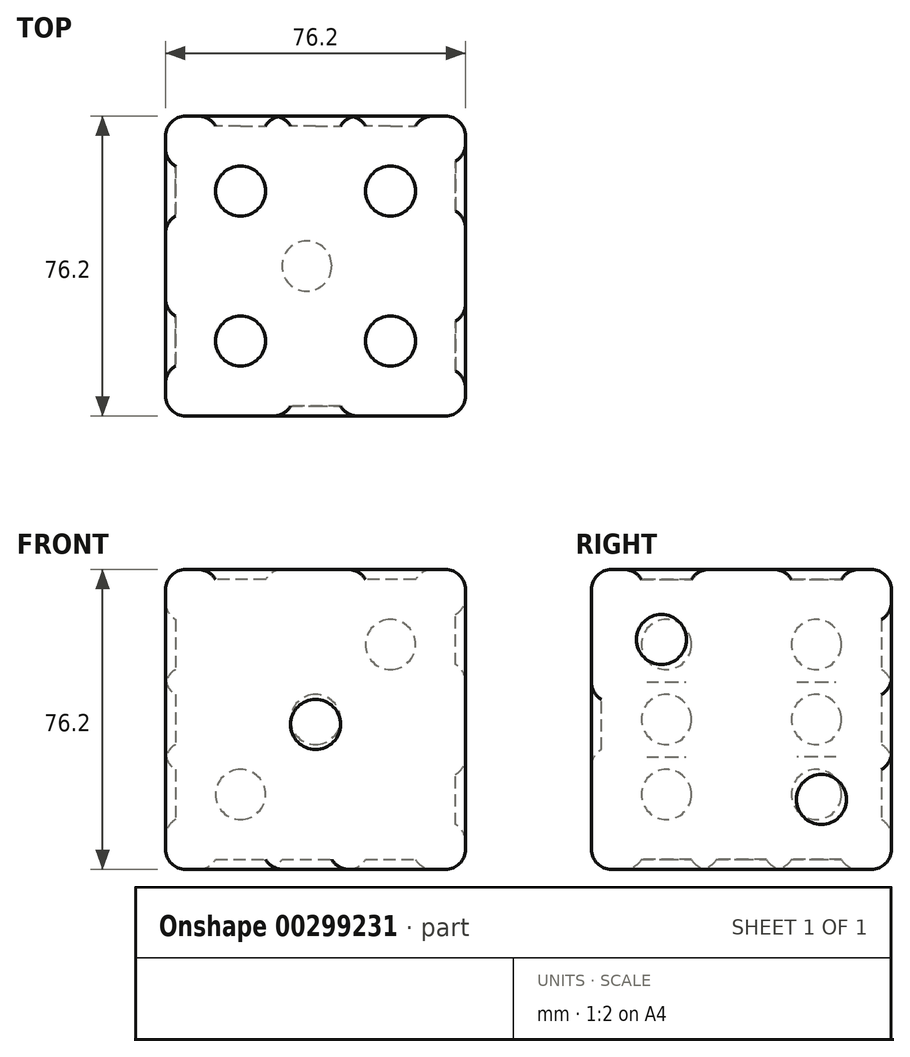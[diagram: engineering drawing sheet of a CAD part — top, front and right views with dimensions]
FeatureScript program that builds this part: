
annotation { "Feature Type Name" : "Feature", "Feature Type Description" : "" }
export const myFeature = defineFeature(function(context is Context, id is Id, definition is map)
    precondition{}
    {
        {
            var Q0;
            Q0=qCreatedBy(makeId("Front.planeOp"),FACE);
            var sketch = newSketch(context, id + "F0", { "sketchPlane" : qUnion([Q0])});
            skLineSegment(sketch, "E0", {"start": v(-45.03, 53.53) * mm, "end": v(31.17, 53.53) * mm});
            skLineSegment(sketch, "E1", {"start": v(31.17, 53.53) * mm, "end": v(31.17, -22.67) * mm});
            skLineSegment(sketch, "E2", {"start": v(31.17, -22.67) * mm, "end": v(-45.03, -22.67) * mm});
            skLineSegment(sketch, "E3", {"start": v(-45.03, -22.67) * mm, "end": v(-45.03, 53.53) * mm});
            skCircle(sketch, "E4", {"center": v(-6.93, 14.16) * mm, "radius": 6.35 * mm});
            skSolve(sketch);
        }
        {
            var Q0;
            Q0 = qSketchRegion(id + "F0", true);
            extrude(context, id + "F1", {"entities" : qUnion([Q0]), "depth" : 76.2 * mm});
        }
        {
            var Q0;
            Q0=makeQuery(id+"F0.imprint","IMPRINT",FACE,{"disambiguationData":[TD([[makeQuery(id+"F0.imprint","IMPRINT",EDGE,{"derivedFrom":sQuery(id+"F0.wireOp",EDGE,"E4")}),1.0]])]});
            extrude(context, id + "F2", {"entities" : qUnion([Q0]), "operationType" : NewBodyOperationType.ADD, "depth" : 73.66 * mm});
        }
        {
            var Q0;
            Q0=makeQuery(id+"F1.opExtrude","SWEPT_FACE",FACE,{"disambiguationData":[OSD([sQuery(id+"F0.wireOp",EDGE,"E1")])]});
            var sketch = newSketch(context, id + "F3", { "sketchPlane" : qUnion([Q0])});
            skCircle(sketch, "E5", {"center": v(-58.42, 35.75) * mm, "radius": 6.35 * mm});
            skCircle(sketch, "E6", {"center": v(-17.78, -4.9) * mm, "radius": 6.35 * mm});
            skSolve(sketch);
        }
        {
            var Q0;
            Q0=makeQuery(id+"F3.imprint","IMPRINT",FACE,{"disambiguationData":[TD([[makeQuery(id+"F3.imprint","IMPRINT",EDGE,{"derivedFrom":sQuery(id+"F3.wireOp",EDGE,"E5")}),1.0]])]});
            extrude(context, id + "F4", {"entities" : qUnion([Q0]), "operationType" : NewBodyOperationType.REMOVE, "oppositeDirection" : true, "depth" : 2.54 * mm});
        }
        {
            var Q0;
            Q0=makeQuery(id+"F3.imprint","IMPRINT",FACE,{"disambiguationData":[TD([[makeQuery(id+"F3.imprint","IMPRINT",EDGE,{"derivedFrom":sQuery(id+"F3.wireOp",EDGE,"E6")}),1.0]])]});
            extrude(context, id + "F5", {"entities" : qUnion([Q0]), "operationType" : NewBodyOperationType.REMOVE, "oppositeDirection" : true, "depth" : 2.54 * mm});
        }
        {
            var Q0;
            {var subQ0=sQuery(id+"F0.wireOp",EDGE,"E4");Q0=makeQuery(id+"F2.boolean.opBoolean","MERGE",FACE,{"derivedFrom":[makeQuery(id+"F1.opExtrude","CAP_FACE",FACE,{"disambiguationData":[OSD([sQuery(id+"F0.wireOp",EDGE,"E0"),sQuery(id+"F0.wireOp",EDGE,"E1"),sQuery(id+"F0.wireOp",EDGE,"E2"),sQuery(id+"F0.wireOp",EDGE,"E3"),subQ0])],"isStart":true}),makeQuery(id+"F2.opExtrude","CAP_FACE",FACE,{"disambiguationData":[OSD([subQ0])],"isStart":true})]});}
            var sketch = newSketch(context, id + "F6", { "sketchPlane" : qUnion([Q0])});
            skCircle(sketch, "E7", {"center": v(6.93, 15.43) * mm, "radius": 6.35 * mm});
            skPoint(sketch, "E7.centerSnap0", {"position": v(45.03, 15.43) * mm});
            skCircle(sketch, "E8", {"center": v(-12.12, 34.48) * mm, "radius": 6.35 * mm});
            skCircle(sketch, "E9", {"center": v(25.98, -3.62) * mm, "radius": 6.35 * mm});
            skSolve(sketch);
        }
        {
            var Q0;
            Q0=makeQuery(id+"F6.imprint","IMPRINT",FACE,{"disambiguationData":[TD([[makeQuery(id+"F6.imprint","IMPRINT",EDGE,{"derivedFrom":sQuery(id+"F6.wireOp",EDGE,"E7")}),1.0]])]});
            extrude(context, id + "F7", {"entities" : qUnion([Q0]), "operationType" : NewBodyOperationType.REMOVE, "oppositeDirection" : true, "depth" : 2.54 * mm});
        }
        {
            var Q0;
            Q0=makeQuery(id+"F6.imprint","IMPRINT",FACE,{"disambiguationData":[TD([[makeQuery(id+"F6.imprint","IMPRINT",EDGE,{"derivedFrom":sQuery(id+"F6.wireOp",EDGE,"E8")}),1.0]])]});
            extrude(context, id + "F8", {"entities" : qUnion([Q0]), "operationType" : NewBodyOperationType.REMOVE, "oppositeDirection" : true, "depth" : 2.54 * mm});
        }
        {
            var Q0;
            Q0=makeQuery(id+"F6.imprint","IMPRINT",FACE,{"disambiguationData":[TD([[makeQuery(id+"F6.imprint","IMPRINT",EDGE,{"derivedFrom":sQuery(id+"F6.wireOp",EDGE,"E9")}),1.0]])]});
            extrude(context, id + "F9", {"entities" : qUnion([Q0]), "operationType" : NewBodyOperationType.REMOVE, "oppositeDirection" : true, "depth" : 2.54 * mm});
        }
        {
            var Q0;
            Q0=makeQuery(id+"F1.opExtrude","SWEPT_FACE",FACE,{"disambiguationData":[OSD([sQuery(id+"F0.wireOp",EDGE,"E0")])]});
            var sketch = newSketch(context, id + "F10", { "sketchPlane" : qUnion([Q0])});
            skCircle(sketch, "E10", {"center": v(-25.98, -19.05) * mm, "radius": 6.35 * mm});
            skCircle(sketch, "E11", {"center": v(12.12, -19.05) * mm, "radius": 6.35 * mm});
            skCircle(sketch, "E12", {"center": v(-25.98, -57.15) * mm, "radius": 6.35 * mm});
            skCircle(sketch, "E13", {"center": v(12.12, -57.15) * mm, "radius": 6.35 * mm});
            skSolve(sketch);
        }
        {
            var Q0;
            Q0=makeQuery(id+"F10.imprint","IMPRINT",FACE,{"disambiguationData":[TD([[makeQuery(id+"F10.imprint","IMPRINT",EDGE,{"derivedFrom":sQuery(id+"F10.wireOp",EDGE,"E10")}),1.0]])]});
            var Q1;
            Q1=makeQuery(id+"F10.imprint","IMPRINT",FACE,{"disambiguationData":[TD([[makeQuery(id+"F10.imprint","IMPRINT",EDGE,{"derivedFrom":sQuery(id+"F10.wireOp",EDGE,"E12")}),1.0]])]});
            var Q2;
            Q2=makeQuery(id+"F10.imprint","IMPRINT",FACE,{"disambiguationData":[TD([[makeQuery(id+"F10.imprint","IMPRINT",EDGE,{"derivedFrom":sQuery(id+"F10.wireOp",EDGE,"E11")}),1.0]])]});
            var Q3;
            Q3=makeQuery(id+"F10.imprint","IMPRINT",FACE,{"disambiguationData":[TD([[makeQuery(id+"F10.imprint","IMPRINT",EDGE,{"derivedFrom":sQuery(id+"F10.wireOp",EDGE,"E13")}),1.0]])]});
            extrude(context, id + "F11", {"entities" : qUnion([Q0, Q1, Q2, Q3]), "operationType" : NewBodyOperationType.REMOVE, "oppositeDirection" : true, "depth" : 2.54 * mm});
        }
        {
            var Q0;
            Q0=makeQuery(id+"F1.opExtrude","SWEPT_FACE",FACE,{"disambiguationData":[OSD([sQuery(id+"F0.wireOp",EDGE,"E2")])]});
            var sketch = newSketch(context, id + "F12", { "sketchPlane" : qUnion([Q0])});
            skCircle(sketch, "E14", {"center": v(-25.98, 57.15) * mm, "radius": 6.35 * mm});
            skCircle(sketch, "E15", {"center": v(-25.98, 19.05) * mm, "radius": 6.35 * mm});
            skCircle(sketch, "E16", {"center": v(12.12, 19.05) * mm, "radius": 6.35 * mm});
            skCircle(sketch, "E17", {"center": v(12.12, 57.15) * mm, "radius": 6.35 * mm});
            skCircle(sketch, "E18", {"center": v(-9.16, 38.1) * mm, "radius": 6.35 * mm});
            skSolve(sketch);
        }
        {
            var Q0;
            Q0=makeQuery(id+"F12.imprint","IMPRINT",FACE,{"disambiguationData":[TD([[makeQuery(id+"F12.imprint","IMPRINT",EDGE,{"derivedFrom":sQuery(id+"F12.wireOp",EDGE,"E14")}),1.0]])]});
            var Q1;
            Q1=makeQuery(id+"F12.imprint","IMPRINT",FACE,{"disambiguationData":[TD([[makeQuery(id+"F12.imprint","IMPRINT",EDGE,{"derivedFrom":sQuery(id+"F12.wireOp",EDGE,"E15")}),1.0]])]});
            var Q2;
            Q2=makeQuery(id+"F12.imprint","IMPRINT",FACE,{"disambiguationData":[TD([[makeQuery(id+"F12.imprint","IMPRINT",EDGE,{"derivedFrom":sQuery(id+"F12.wireOp",EDGE,"E18")}),1.0]])]});
            var Q3;
            Q3=makeQuery(id+"F12.imprint","IMPRINT",FACE,{"disambiguationData":[TD([[makeQuery(id+"F12.imprint","IMPRINT",EDGE,{"derivedFrom":sQuery(id+"F12.wireOp",EDGE,"E17")}),1.0]])]});
            var Q4;
            Q4=makeQuery(id+"F12.imprint","IMPRINT",FACE,{"disambiguationData":[TD([[makeQuery(id+"F12.imprint","IMPRINT",EDGE,{"derivedFrom":sQuery(id+"F12.wireOp",EDGE,"E16")}),1.0]])]});
            extrude(context, id + "F13", {"entities" : qUnion([Q0, Q1, Q2, Q3, Q4]), "operationType" : NewBodyOperationType.REMOVE, "oppositeDirection" : true, "depth" : 2.54 * mm});
        }
        {
            var Q0;
            Q0=makeQuery(id+"F1.opExtrude","SWEPT_FACE",FACE,{"disambiguationData":[OSD([sQuery(id+"F0.wireOp",EDGE,"E3")])]});
            var sketch = newSketch(context, id + "F14", { "sketchPlane" : qUnion([Q0])});
            skCircle(sketch, "E19", {"center": v(19.05, 34.48) * mm, "radius": 6.35 * mm});
            skCircle(sketch, "E20", {"center": v(19.05, -3.62) * mm, "radius": 6.35 * mm});
            skCircle(sketch, "E21", {"center": v(19.05, 15.43) * mm, "radius": 6.35 * mm});
            skCircle(sketch, "E22", {"center": v(57.15, 34.48) * mm, "radius": 6.35 * mm});
            skCircle(sketch, "E23", {"center": v(57.15, -3.62) * mm, "radius": 6.35 * mm});
            skCircle(sketch, "E24", {"center": v(57.15, 15.43) * mm, "radius": 6.35 * mm});
            skSolve(sketch);
        }
        {
            var Q0;
            Q0=makeQuery(id+"F14.imprint","IMPRINT",FACE,{"disambiguationData":[TD([[makeQuery(id+"F14.imprint","IMPRINT",EDGE,{"derivedFrom":sQuery(id+"F14.wireOp",EDGE,"E20")}),1.0]])]});
            var Q1;
            Q1=makeQuery(id+"F14.imprint","IMPRINT",FACE,{"disambiguationData":[TD([[makeQuery(id+"F14.imprint","IMPRINT",EDGE,{"derivedFrom":sQuery(id+"F14.wireOp",EDGE,"E21")}),1.0]])]});
            var Q2;
            Q2=makeQuery(id+"F14.imprint","IMPRINT",FACE,{"disambiguationData":[TD([[makeQuery(id+"F14.imprint","IMPRINT",EDGE,{"derivedFrom":sQuery(id+"F14.wireOp",EDGE,"E19")}),1.0]])]});
            var Q3;
            Q3=makeQuery(id+"F14.imprint","IMPRINT",FACE,{"disambiguationData":[TD([[makeQuery(id+"F14.imprint","IMPRINT",EDGE,{"derivedFrom":sQuery(id+"F14.wireOp",EDGE,"E22")}),1.0]])]});
            var Q4;
            Q4=makeQuery(id+"F14.imprint","IMPRINT",FACE,{"disambiguationData":[TD([[makeQuery(id+"F14.imprint","IMPRINT",EDGE,{"derivedFrom":sQuery(id+"F14.wireOp",EDGE,"E24")}),1.0]])]});
            var Q5;
            Q5=makeQuery(id+"F14.imprint","IMPRINT",FACE,{"disambiguationData":[TD([[makeQuery(id+"F14.imprint","IMPRINT",EDGE,{"derivedFrom":sQuery(id+"F14.wireOp",EDGE,"E23")}),1.0]])]});
            extrude(context, id + "F15", {"entities" : qUnion([Q0, Q1, Q2, Q3, Q4, Q5]), "operationType" : NewBodyOperationType.REMOVE, "oppositeDirection" : true, "depth" : 2.54 * mm});
        }
        {
            var Q0;
            {var subQ0=sQuery(id+"F0.wireOp",EDGE,"E4");Q0=makeQuery(id+"F2.boolean.opBoolean","MERGE",FACE,{"derivedFrom":[makeQuery(id+"F1.opExtrude","CAP_FACE",FACE,{"disambiguationData":[OSD([sQuery(id+"F0.wireOp",EDGE,"E0"),sQuery(id+"F0.wireOp",EDGE,"E1"),sQuery(id+"F0.wireOp",EDGE,"E2"),sQuery(id+"F0.wireOp",EDGE,"E3"),subQ0])],"isStart":true}),makeQuery(id+"F2.opExtrude","CAP_FACE",FACE,{"disambiguationData":[OSD([subQ0])],"isStart":true})]});}
            var Q1;
            Q1=makeQuery(id+"F1.opExtrude","SWEPT_FACE",FACE,{"disambiguationData":[OSD([sQuery(id+"F0.wireOp",EDGE,"E1")])]});
            var Q2;
            Q2=makeQuery(id+"F1.opExtrude","SWEPT_FACE",FACE,{"disambiguationData":[OSD([sQuery(id+"F0.wireOp",EDGE,"E0")])]});
            var Q3;
            Q3=makeQuery(id+"F1.opExtrude","SWEPT_FACE",FACE,{"disambiguationData":[OSD([sQuery(id+"F0.wireOp",EDGE,"E3")])]});
            var Q4;
            Q4=makeQuery(id+"F1.opExtrude","CAP_FACE",FACE,{"disambiguationData":[OSD([sQuery(id+"F0.wireOp",EDGE,"E0"),sQuery(id+"F0.wireOp",EDGE,"E1"),sQuery(id+"F0.wireOp",EDGE,"E2"),sQuery(id+"F0.wireOp",EDGE,"E3"),sQuery(id+"F0.wireOp",EDGE,"E4")])],"isStart":false});
            var Q5;
            Q5=makeQuery(id+"F1.opExtrude","SWEPT_FACE",FACE,{"disambiguationData":[OSD([sQuery(id+"F0.wireOp",EDGE,"E2")])]});
            fillet(context, id + "F16", {"entities" : qUnion([Q0, Q1, Q2, Q3, Q4, Q5]), "radius" : 5.08 * mm, "tangentPropagation" : true, "allowEdgeOverflow" : false});
        }
    });
